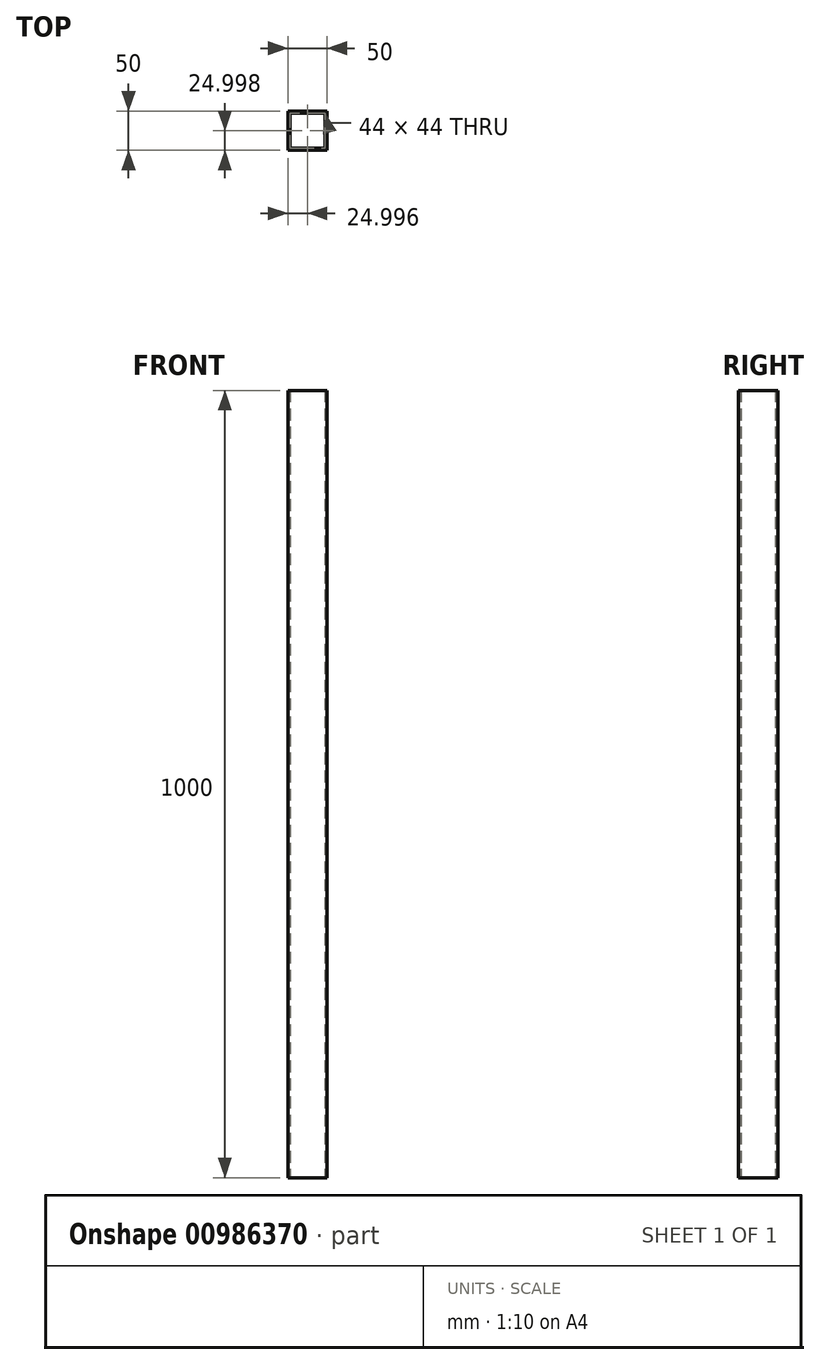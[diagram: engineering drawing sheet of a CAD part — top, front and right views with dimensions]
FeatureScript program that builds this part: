
annotation { "Feature Type Name" : "Feature", "Feature Type Description" : "" }
export const myFeature = defineFeature(function(context is Context, id is Id, definition is map)
    precondition{}
    {
        {
            var Q0;
            Q0=qCreatedBy(makeId("Top.planeOp"),FACE);
            var sketch = newSketch(context, id + "F0", { "sketchPlane" : qUnion([Q0])});
            skLineSegment(sketch, "E0.bottom", {"start": v(-48.15, 63.7) * mm, "end": v(1.85, 63.7) * mm});
            skLineSegment(sketch, "E0.top", {"start": v(-48.15, 13.7) * mm, "end": v(1.85, 13.7) * mm});
            skLineSegment(sketch, "E0.left", {"start": v(-48.15, 63.7) * mm, "end": v(-48.15, 13.7) * mm});
            skLineSegment(sketch, "E0.right", {"start": v(1.85, 63.7) * mm, "end": v(1.85, 13.7) * mm});
            skLineSegment(sketch, "E1.0", {"start": v(-45.15, 60.7) * mm, "end": v(-1.15, 60.7) * mm});
            skLineSegment(sketch, "E1.1", {"start": v(-45.15, 60.7) * mm, "end": v(-45.15, 16.7) * mm});
            skLineSegment(sketch, "E1.2", {"start": v(-45.15, 16.7) * mm, "end": v(-1.15, 16.7) * mm});
            skLineSegment(sketch, "E1.3", {"start": v(-1.15, 60.7) * mm, "end": v(-1.15, 16.7) * mm});
            skSolve(sketch);
        }
        {
            var Q0;
            Q0=makeQuery(id+"F0.imprint","IMPRINT",FACE,{"disambiguationData":[TD([[makeQuery(id+"F0.imprint","IMPRINT",EDGE,{"derivedFrom":sQuery(id+"F0.wireOp",EDGE,"E0.bottom")}),-1.0]])]});
            extrude(context, id + "F1", {"entities" : qUnion([Q0]), "depth" : 1000 * mm, "offsetDistance" : 25 * mm});
        }
    });
